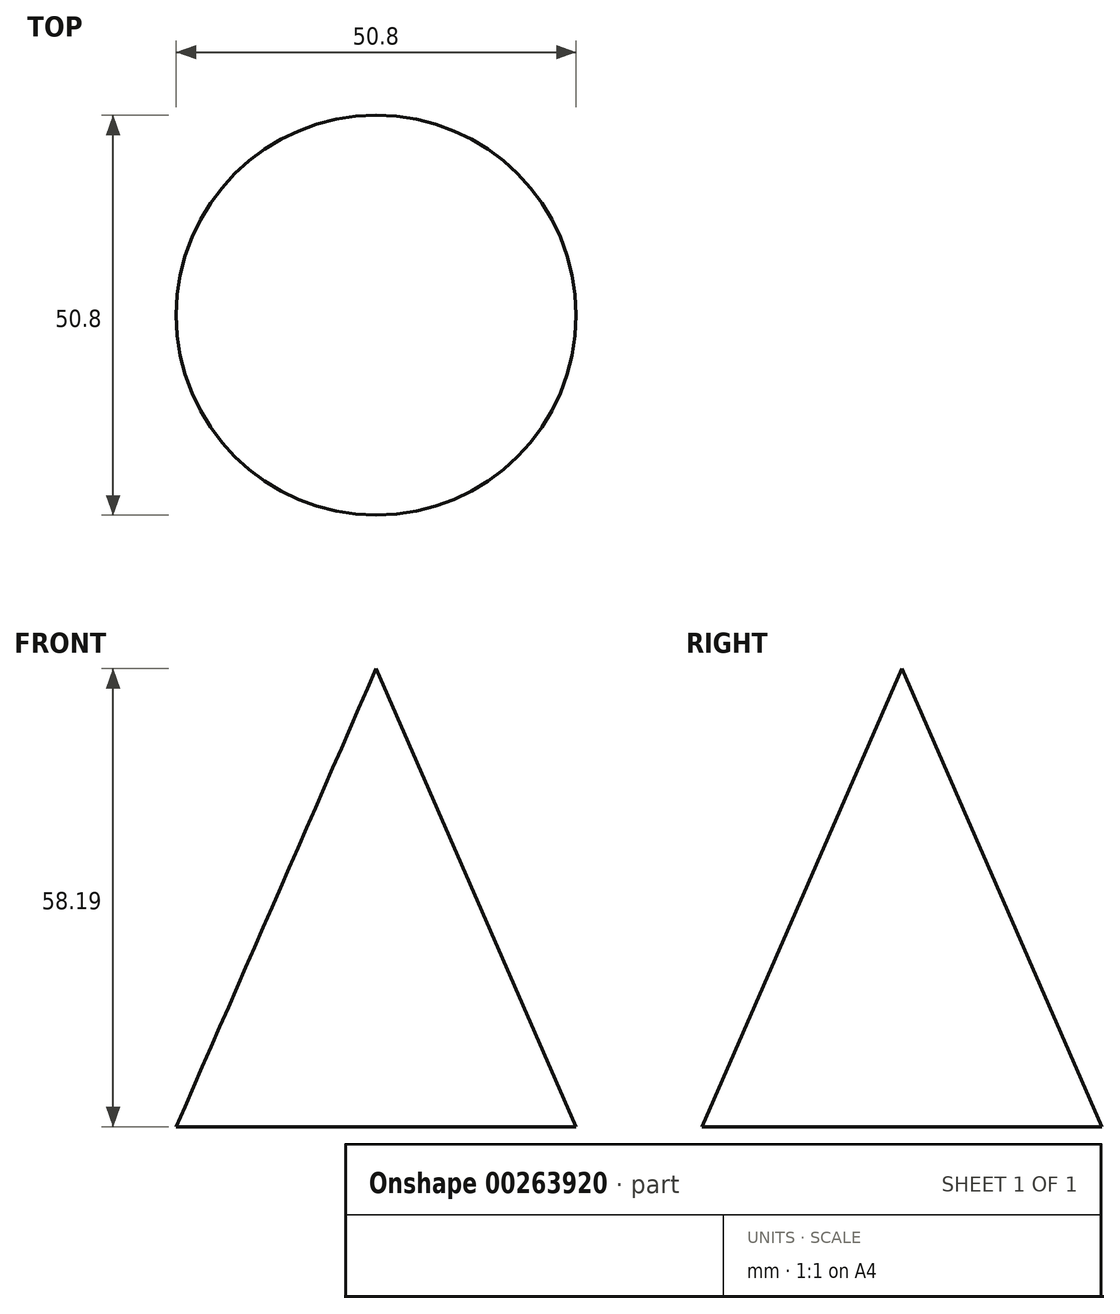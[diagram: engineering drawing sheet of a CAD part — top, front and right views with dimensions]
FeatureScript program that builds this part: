
annotation { "Feature Type Name" : "Feature", "Feature Type Description" : "" }
export const myFeature = defineFeature(function(context is Context, id is Id, definition is map)
    precondition{}
    {
        {
            var Q0;
            Q0=qCreatedBy(makeId("Front.planeOp"),FACE);
            var sketch = newSketch(context, id + "F0", { "sketchPlane" : qUnion([Q0])});
            skLineSegment(sketch, "E0", {"start": v(0, -30.64) * mm, "end": v(25.4, -30.64) * mm});
            skLineSegment(sketch, "E1", {"start": v(25.4, -30.64) * mm, "end": v(0, 27.55) * mm});
            skLineSegment(sketch, "E2", {"start": v(0, 27.55) * mm, "end": v(0, -30.64) * mm});
            skSolve(sketch);
        }
        {
            var Q0;
            Q0 = qSketchRegion(id + "F0", true);
            var Q1;
            Q1=sQuery(id+"F0.wireOp",EDGE,"E2");
            revolve(context, id + "F1", {"entities" : qUnion([Q0]), "axis" : qUnion([Q1]), "revolveType" : RevolveType.FULL});
        }
    });
